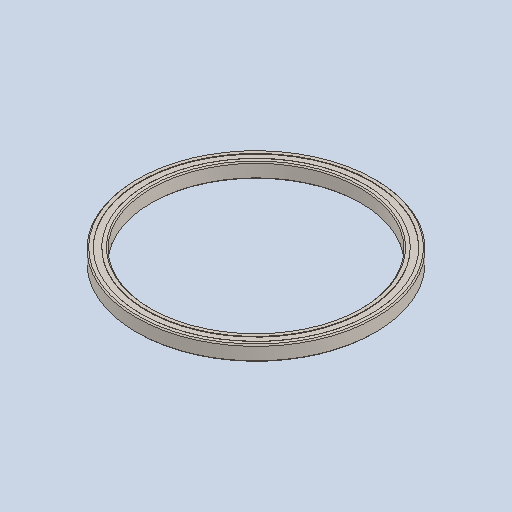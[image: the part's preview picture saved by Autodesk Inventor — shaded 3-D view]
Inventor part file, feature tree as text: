
AUTODESK INVENTOR PART (.ipt)
format: ipt  version: 2023.2 (Build 272271000, 271)  size: 128,512 bytes
history: native  units: in
note: dims shown in document units (in); Inventor stores cm internally (conversion verified against a paired STEP export)
features: revolve x1
ambient origin geometry x8: Origin, YZ Plane, XZ Plane, XY Plane, X Axis, Y Axis, Z Axis, Center Point
bodies: Solid1 (feature_tree)
feature tree (1):
  revolve  "Revolve1"  [1 undecoded]
note: 1 required parameter value undecoded (feature->parameter linkage not recoverable at this tier; creation-order binding heuristic only, values carry confidence <= 0.55)
